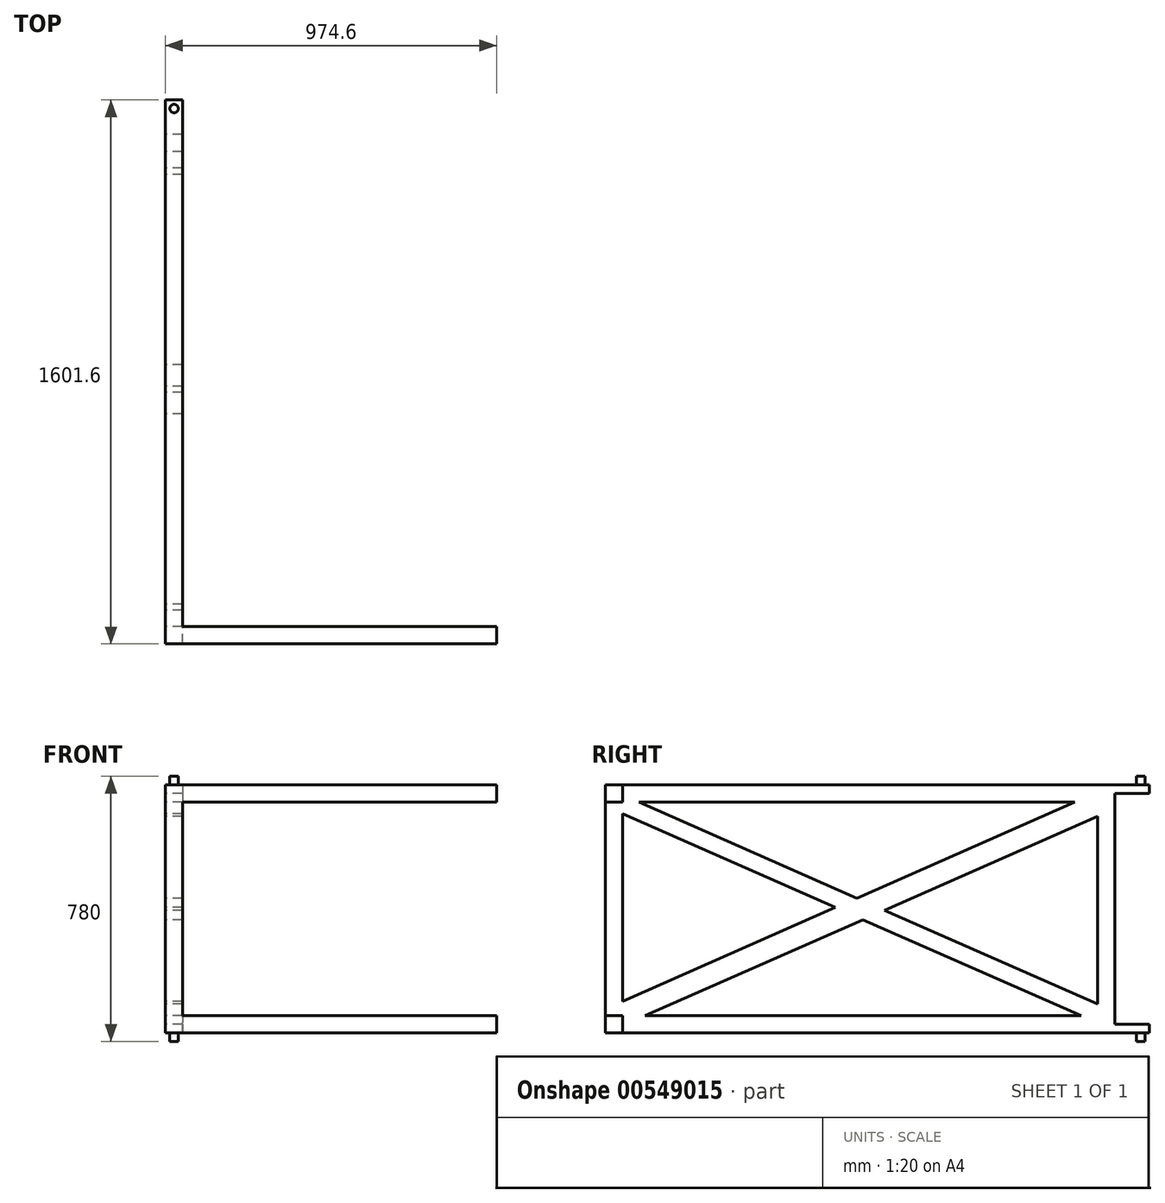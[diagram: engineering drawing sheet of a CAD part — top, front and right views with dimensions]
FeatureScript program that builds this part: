
annotation { "Feature Type Name" : "Feature", "Feature Type Description" : "" }
export const myFeature = defineFeature(function(context is Context, id is Id, definition is map)
    precondition{}
    {
        {
            var Q0;
            Q0=qCreatedBy(makeId("Right.planeOp"),FACE);
            var sketch = newSketch(context, id + "F0", { "sketchPlane" : qUnion([Q0])});
            skLineSegment(sketch, "E0.bottom", {"start": v(0, 730) * mm, "end": v(-1500, 730) * mm});
            skLineSegment(sketch, "E0.top", {"start": v(0, 0) * mm, "end": v(-1500, 0) * mm});
            skLineSegment(sketch, "E0.left", {"start": v(0, 730) * mm, "end": v(0, 0) * mm});
            skLineSegment(sketch, "E0.right", {"start": v(-1500, 730) * mm, "end": v(-1500, 0) * mm});
            skLineSegment(sketch, "E1.0", {"start": v(-50.8, 50.8) * mm, "end": v(-1449.2, 50.8) * mm});
            skLineSegment(sketch, "E1.1", {"start": v(-50.8, 679.2) * mm, "end": v(-50.8, 50.8) * mm});
            skLineSegment(sketch, "E1.2", {"start": v(-50.8, 679.2) * mm, "end": v(-1449.2, 679.2) * mm});
            skLineSegment(sketch, "E1.3", {"start": v(-1449.2, 679.2) * mm, "end": v(-1449.2, 50.8) * mm});
            skSolve(sketch);
        }
        {
            var Q0;
            Q0=makeQuery(id+"F0.imprint","IMPRINT",FACE,{"disambiguationData":[TD([[makeQuery(id+"F0.imprint","IMPRINT",EDGE,{"derivedFrom":sQuery(id+"F0.wireOp",EDGE,"E0.bottom")}),1.0]])]});
            extrude(context, id + "F1", {"entities" : qUnion([Q0]), "depth" : 50.8 * mm, "offsetDistance" : 25 * mm});
        }
        {
            var Q0;
            Q0=makeQuery(id+"F1.opExtrude","CAP_FACE",FACE,{"disambiguationData":[OSD([sQuery(id+"F0.wireOp",EDGE,"E0.bottom"),sQuery(id+"F0.wireOp",EDGE,"E0.top"),sQuery(id+"F0.wireOp",EDGE,"E0.left"),sQuery(id+"F0.wireOp",EDGE,"E0.right"),sQuery(id+"F0.wireOp",EDGE,"E1.0"),sQuery(id+"F0.wireOp",EDGE,"E1.1"),sQuery(id+"F0.wireOp",EDGE,"E1.2"),sQuery(id+"F0.wireOp",EDGE,"E1.3")])],"isStart":true});
            var sketch = newSketch(context, id + "F2", { "sketchPlane" : qUnion([Q0])});
            skLineSegment(sketch, "E2.0", {"start": v(117.18, 679.2) * mm, "end": v(759.04, 396.73) * mm});
            skLineSegment(sketch, "E3.0", {"start": v(50.8, 637) * mm, "end": v(677.9, 361.02) * mm});
            skLineSegment(sketch, "E4.0", {"start": v(1449.2, 644.96) * mm, "end": v(822.1, 368.98) * mm});
            skLineSegment(sketch, "E5.0", {"start": v(1400.9, 679.2) * mm, "end": v(759.04, 396.73) * mm});
            skLineSegment(sketch, "E6.0", {"start": v(50.8, 679.2) * mm, "end": v(50.8, 50.8) * mm});
            skLineSegment(sketch, "E7.0.0", {"start": v(0, 0) * mm, "end": v(1500, 0) * mm});
            skLineSegment(sketch, "E7.0.1", {"start": v(1500, 0) * mm, "end": v(1500, 730) * mm});
            skLineSegment(sketch, "E7.0.2", {"start": v(1500, 730) * mm, "end": v(0, 730) * mm});
            skLineSegment(sketch, "E7.0.3", {"start": v(0, 730) * mm, "end": v(0, 0) * mm});
            skLineSegment(sketch, "E8.0", {"start": v(50.8, 50.8) * mm, "end": v(1449.2, 50.8) * mm});
            skLineSegment(sketch, "E9.0", {"start": v(1449.2, 679.2) * mm, "end": v(1449.2, 50.8) * mm});
            skLineSegment(sketch, "E10.0", {"start": v(50.8, 679.2) * mm, "end": v(1449.2, 679.2) * mm});
            skLineSegment(sketch, "E11.trimOffspring", {"start": v(740.96, 333.27) * mm, "end": v(1382.82, 50.8) * mm});
            skLineSegment(sketch, "E12.trimOffspring", {"start": v(677.9, 361.02) * mm, "end": v(50.8, 85.04) * mm});
            skLineSegment(sketch, "E13.trimOffspring", {"start": v(822.1, 368.98) * mm, "end": v(1449.2, 93) * mm});
            skLineSegment(sketch, "E14.trimOffspring", {"start": v(740.96, 333.27) * mm, "end": v(99.1, 50.8) * mm});
            skSolve(sketch);
        }
        {
            var Q0;
            {var subQ11=sQuery(id+"F2.wireOp",EDGE,"E2.0");Q0=makeQuery(id+"F2.imprint","IMPRINT",FACE,{"disambiguationData":[TD([[makeQuery(id+"F2.imprint","IMPRINT",EDGE,{"derivedFrom":subQ11}),-1.0]])]});}
            var Q1;
            Q1=makeQuery(id+"F1.opExtrude","CAP_FACE",FACE,{"disambiguationData":[OSD([sQuery(id+"F0.wireOp",EDGE,"E0.bottom"),sQuery(id+"F0.wireOp",EDGE,"E0.top"),sQuery(id+"F0.wireOp",EDGE,"E0.left"),sQuery(id+"F0.wireOp",EDGE,"E0.right"),sQuery(id+"F0.wireOp",EDGE,"E1.0"),sQuery(id+"F0.wireOp",EDGE,"E1.1"),sQuery(id+"F0.wireOp",EDGE,"E1.2"),sQuery(id+"F0.wireOp",EDGE,"E1.3")])],"isStart":false});
            extrude(context, id + "F3", {"entities" : qUnion([Q0]), "operationType" : NewBodyOperationType.ADD, "endBound" : BoundingType.UP_TO_SURFACE, "oppositeDirection" : true, "depth" : 25 * mm, "endBoundEntityFace" : qUnion([Q1]), "offsetDistance" : 25 * mm});
        }
        {
            var Q0;
            Q0=makeQuery(id+"F1.opExtrude","SWEPT_FACE",FACE,{"disambiguationData":[OSD([sQuery(id+"F0.wireOp",EDGE,"E0.left")])]});
            var sketch = newSketch(context, id + "F4", { "sketchPlane" : qUnion([Q0])});
            skLineSegment(sketch, "E15.bottom", {"start": v(-50.8, 730) * mm, "end": v(0, 730) * mm});
            skLineSegment(sketch, "E15.top", {"start": v(-50.8, 704.6) * mm, "end": v(0, 704.6) * mm});
            skLineSegment(sketch, "E15.left", {"start": v(-50.8, 730) * mm, "end": v(-50.8, 704.6) * mm});
            skLineSegment(sketch, "E15.right", {"start": v(0, 730) * mm, "end": v(0, 704.6) * mm});
            skLineSegment(sketch, "E16.bottom", {"start": v(-50.8, 0) * mm, "end": v(0, 0) * mm});
            skLineSegment(sketch, "E16.top", {"start": v(-50.8, 25.4) * mm, "end": v(0, 25.4) * mm});
            skLineSegment(sketch, "E16.left", {"start": v(-50.8, 0) * mm, "end": v(-50.8, 25.4) * mm});
            skLineSegment(sketch, "E16.right", {"start": v(0, 0) * mm, "end": v(0, 25.4) * mm});
            skSolve(sketch);
        }
        {
            var Q0;
            Q0=makeQuery(id+"F4.imprint","IMPRINT",FACE,{"disambiguationData":[TD([[makeQuery(id+"F4.imprint","IMPRINT",EDGE,{"derivedFrom":sQuery(id+"F4.wireOp",EDGE,"E15.bottom")}),-1.0]])]});
            var Q1;
            Q1=makeQuery(id+"F4.imprint","IMPRINT",FACE,{"disambiguationData":[TD([[makeQuery(id+"F4.imprint","IMPRINT",EDGE,{"derivedFrom":sQuery(id+"F4.wireOp",EDGE,"E16.bottom")}),1.0]])]});
            extrude(context, id + "F5", {"entities" : qUnion([Q0, Q1]), "operationType" : NewBodyOperationType.ADD, "depth" : 101.6 * mm, "offsetDistance" : 25 * mm});
        }
        {
            var Q0;
            Q0=makeQuery(id+"F5.boolean.opBoolean","MERGE",FACE,{"derivedFrom":[makeQuery(id+"F1.opExtrude","SWEPT_FACE",FACE,{"disambiguationData":[OSD([sQuery(id+"F0.wireOp",EDGE,"E0.bottom")])]}),makeQuery(id+"F5.opExtrude","SWEPT_FACE",FACE,{"disambiguationData":[OSD([sQuery(id+"F4.wireOp",EDGE,"E15.bottom")])]})]});
            var sketch = newSketch(context, id + "F6", { "sketchPlane" : qUnion([Q0])});
            skCircle(sketch, "E17", {"center": v(25.4, 76.2) * mm, "radius": 12.5 * mm});
            skPoint(sketch, "E17.centerSnap0", {"position": v(25.4, 101.6) * mm});
            skSolve(sketch);
        }
        {
            var Q0;
            Q0=makeQuery(id+"F6.imprint","IMPRINT",FACE,{"disambiguationData":[TD([[makeQuery(id+"F6.imprint","IMPRINT",EDGE,{"derivedFrom":sQuery(id+"F6.wireOp",EDGE,"E17")}),1.0]])]});
            extrude(context, id + "F7", {"entities" : qUnion([Q0]), "operationType" : NewBodyOperationType.ADD, "depth" : 25 * mm, "offsetDistance" : 25 * mm});
        }
        {
            var Q0;
            Q0=makeQuery(id+"F5.boolean.opBoolean","MERGE",FACE,{"derivedFrom":[makeQuery(id+"F1.opExtrude","SWEPT_FACE",FACE,{"disambiguationData":[OSD([sQuery(id+"F0.wireOp",EDGE,"E0.top")])]}),makeQuery(id+"F5.opExtrude","SWEPT_FACE",FACE,{"disambiguationData":[OSD([sQuery(id+"F4.wireOp",EDGE,"E16.bottom")])]})]});
            var sketch = newSketch(context, id + "F8", { "sketchPlane" : qUnion([Q0])});
            skCircle(sketch, "E18.0", {"center": v(25.4, -76.2) * mm, "radius": 12.5 * mm});
            skSolve(sketch);
        }
        {
            var Q0;
            Q0=makeQuery(id+"F8.imprint","IMPRINT",FACE,{"disambiguationData":[TD([[makeQuery(id+"F8.imprint","IMPRINT",EDGE,{"derivedFrom":sQuery(id+"F8.wireOp",EDGE,"E18.0")}),1.0]])]});
            extrude(context, id + "F9", {"entities" : qUnion([Q0]), "operationType" : NewBodyOperationType.ADD, "depth" : 25 * mm, "offsetDistance" : 25 * mm});
        }
        {
            var Q0;
            {var subQ0=sQuery(id+"F0.wireOp",EDGE,"E1.3");var subQ1=sQuery(id+"F0.wireOp",EDGE,"E1.2");var subQ2=sQuery(id+"F0.wireOp",EDGE,"E1.1");var subQ3=sQuery(id+"F0.wireOp",EDGE,"E1.0");var subQ4=sQuery(id+"F0.wireOp",EDGE,"E0.right");var subQ5=sQuery(id+"F0.wireOp",EDGE,"E0.left");var subQ6=sQuery(id+"F0.wireOp",EDGE,"E0.top");var subQ7=sQuery(id+"F0.wireOp",EDGE,"E0.bottom");Q0=makeQuery(id+"F5.boolean.opBoolean","MERGE",FACE,{"derivedFrom":[makeQuery(id+"F3.boolean.opBoolean","MERGE",FACE,{"derivedFrom":[makeQuery(id+"F1.opExtrude","CAP_FACE",FACE,{"disambiguationData":[OSD([subQ7,subQ6,subQ5,subQ4,subQ3,subQ2,subQ1,subQ0])],"isStart":false}),makeQuery(id+"F3.opExtrude","CAP_FACE",FACE,{"disambiguationData":[OSD([subQ7,subQ6,subQ5,subQ4,subQ3,subQ2,subQ1,subQ0])],"isStart":false})]}),makeQuery(id+"F5.opExtrude","SWEPT_FACE",FACE,{"disambiguationData":[OSD([sQuery(id+"F4.wireOp",EDGE,"E15.left")])]}),makeQuery(id+"F5.opExtrude","SWEPT_FACE",FACE,{"disambiguationData":[OSD([sQuery(id+"F4.wireOp",EDGE,"E16.left")])]})]});}
            var sketch = newSketch(context, id + "F10", { "sketchPlane" : qUnion([Q0])});
            skLineSegment(sketch, "E19.bottom", {"start": v(-1500, 0) * mm, "end": v(-1449.2, 0) * mm});
            skLineSegment(sketch, "E19.top", {"start": v(-1500, 50.8) * mm, "end": v(-1449.2, 50.8) * mm});
            skLineSegment(sketch, "E19.left", {"start": v(-1500, 0) * mm, "end": v(-1500, 50.8) * mm});
            skLineSegment(sketch, "E19.right", {"start": v(-1449.2, 0) * mm, "end": v(-1449.2, 50.8) * mm});
            skLineSegment(sketch, "E20.bottom", {"start": v(-1500, 730) * mm, "end": v(-1449.2, 730) * mm});
            skLineSegment(sketch, "E20.top", {"start": v(-1500, 679.2) * mm, "end": v(-1449.2, 679.2) * mm});
            skLineSegment(sketch, "E20.left", {"start": v(-1500, 730) * mm, "end": v(-1500, 679.2) * mm});
            skLineSegment(sketch, "E20.right", {"start": v(-1449.2, 730) * mm, "end": v(-1449.2, 679.2) * mm});
            skSolve(sketch);
        }
        {
            var Q0;
            Q0=makeQuery(id+"F10.imprint","IMPRINT",FACE,{"disambiguationData":[TD([[makeQuery(id+"F10.imprint","IMPRINT",EDGE,{"derivedFrom":sQuery(id+"F10.wireOp",EDGE,"E20.bottom")}),1.0]])]});
            var Q1;
            Q1=makeQuery(id+"F10.imprint","IMPRINT",FACE,{"disambiguationData":[TD([[makeQuery(id+"F10.imprint","IMPRINT",EDGE,{"derivedFrom":sQuery(id+"F10.wireOp",EDGE,"E19.bottom")}),-1.0]])]});
            extrude(context, id + "F11", {"entities" : qUnion([Q0, Q1]), "operationType" : NewBodyOperationType.ADD, "depth" : (2000 * mm - 152.4 * mm) / 2, "offsetDistance" : 25 * mm});
        }
    });
